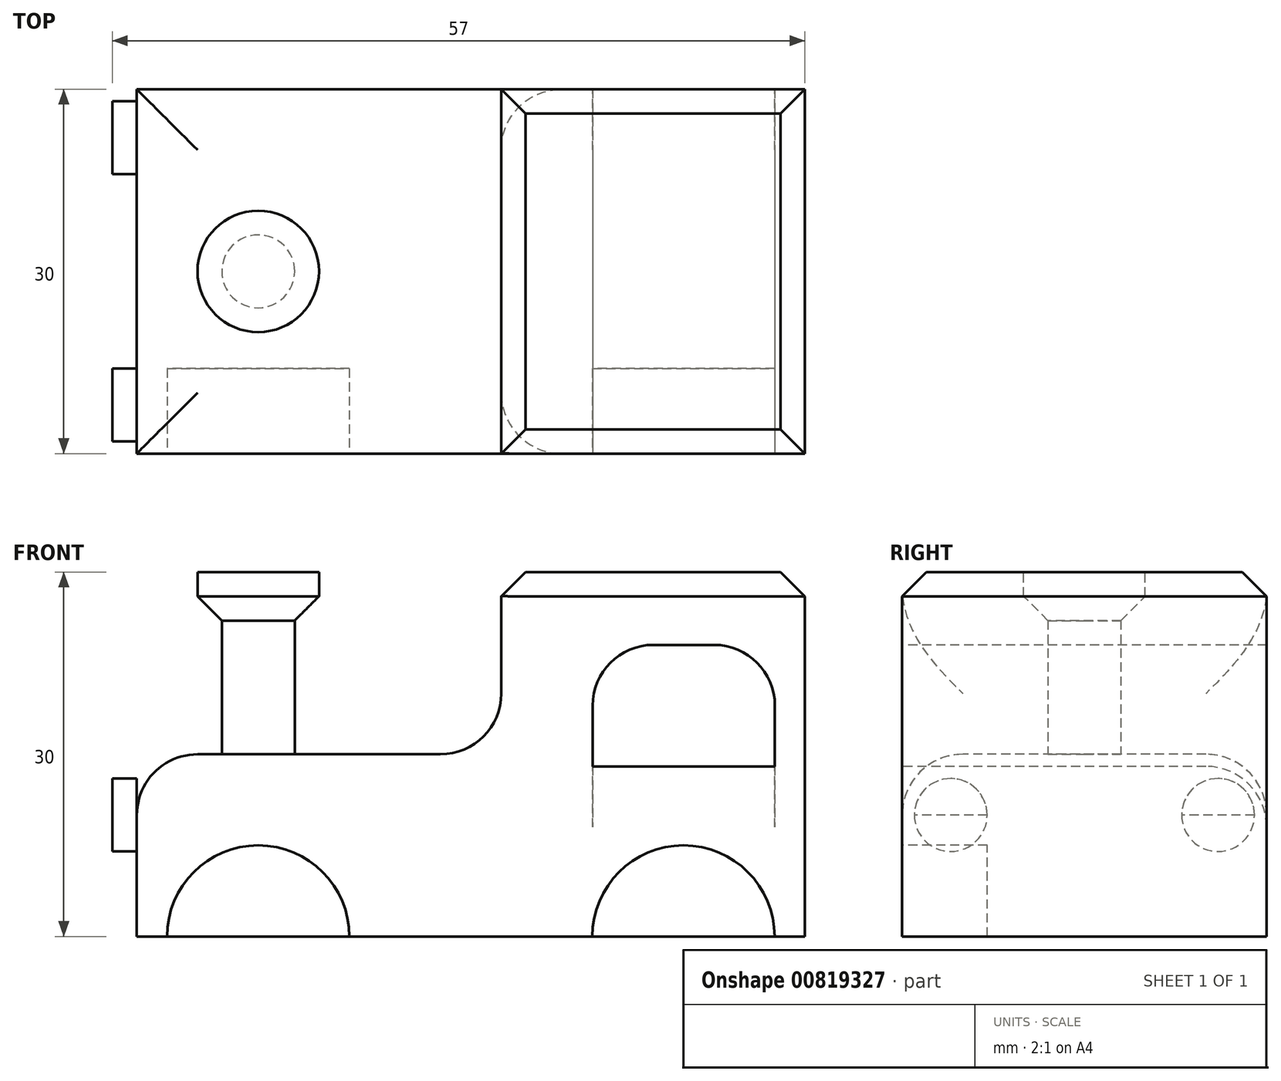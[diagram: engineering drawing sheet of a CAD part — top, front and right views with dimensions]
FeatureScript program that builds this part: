
annotation { "Feature Type Name" : "Feature", "Feature Type Description" : "" }
export const myFeature = defineFeature(function(context is Context, id is Id, definition is map)
    precondition{}
    {
        {
            var Q0;
            Q0=qCreatedBy(makeId("Top.planeOp"),FACE);
            var sketch = newSketch(context, id + "F0", { "sketchPlane" : qUnion([Q0])});
            skLineSegment(sketch, "E0.bottom", {"start": v(-27.5, 15) * mm, "end": v(27.5, 15) * mm});
            skLineSegment(sketch, "E0.top", {"start": v(-27.5, -15) * mm, "end": v(27.5, -15) * mm});
            skLineSegment(sketch, "E0.left", {"start": v(-27.5, 15) * mm, "end": v(-27.5, -15) * mm});
            skLineSegment(sketch, "E0.right", {"start": v(27.5, 15) * mm, "end": v(27.5, -15) * mm});
            skPoint(sketch, "E0.middle", {"position": v(0, 0) * mm});
            skSolve(sketch);
        }
        {
            var Q0;
            Q0 = qSketchRegion(id + "F0", true);
            extrude(context, id + "F1", {"entities" : qUnion([Q0]), "depth" : 30 * mm, "offsetDistance" : 25 * mm});
        }
        {
            var Q0;
            Q0=makeQuery(id+"F1.opExtrude","SWEPT_FACE",FACE,{"disambiguationData":[OSD([sQuery(id+"F0.wireOp",EDGE,"E0.top")])]});
            var sketch = newSketch(context, id + "F2", { "sketchPlane" : qUnion([Q0])});
            skLineSegment(sketch, "E1", {"start": v(-27.5, 15) * mm, "end": v(-27.5, 0) * mm});
            skLineSegment(sketch, "E2", {"start": v(-27.5, 0) * mm, "end": v(27.5, 0) * mm});
            skLineSegment(sketch, "E3", {"start": v(27.5, 0) * mm, "end": v(27.5, 30) * mm});
            skLineSegment(sketch, "E4", {"start": v(27.5, 30) * mm, "end": v(2.5, 30) * mm});
            skLineSegment(sketch, "E5", {"start": v(2.5, 30) * mm, "end": v(2.5, 15) * mm});
            skLineSegment(sketch, "E6", {"start": v(2.5, 15) * mm, "end": v(-27.5, 15) * mm});
            skSolve(sketch);
        }
        {
            var Q0;
            {var subQ0=sQuery(id+"F2.wireOp",EDGE,"E5");Q0=makeQuery(id+"F2.imprint","IMPRINT",FACE,{"disambiguationData":[TD([[makeQuery(id+"F2.imprint","IMPRINT",EDGE,{"derivedFrom":subQ0}),-1.0]])]});}
            extrude(context, id + "F3", {"entities" : qUnion([Q0]), "operationType" : NewBodyOperationType.REMOVE, "endBound" : BoundingType.THROUGH_ALL, "oppositeDirection" : true, "depth" : 25 * mm, "offsetDistance" : 25 * mm});
        }
        {
            var Q0;
            Q0=makeQuery(id+"F1.opExtrude","SWEPT_FACE",FACE,{"disambiguationData":[OSD([sQuery(id+"F0.wireOp",EDGE,"E0.top")])]});
            var sketch = newSketch(context, id + "F4", { "sketchPlane" : qUnion([Q0])});
            skCircle(sketch, "E7", {"center": v(-17.5, 0) * mm, "radius": 7.5 * mm});
            skCircle(sketch, "E8.1.0.0", {"center": v(17.5, 0) * mm, "radius": 7.5 * mm});
            skLineSegment(sketch, "E8.direction1", {"start": v(-17.5, 0) * mm, "end": v(17.5, 0) * mm, "construction": true});
            skSolve(sketch);
        }
        {
            var Q0;
            {var subQ0=sQuery(id+"F4.wireOp",EDGE,"E7");var subQ1=makeQuery(id+"F1.opExtrude","CAP_EDGE",EDGE,{"disambiguationData":[OSD([sQuery(id+"F0.wireOp",EDGE,"E0.top")])],"isStart":true});var subQ2=makeQuery(id+"F4.imprint","INTERSECT",VERTEX,{"disambiguationData":[OD(0.0)],"derivedFrom":[subQ1,subQ0]});Q0=makeQuery(id+"F4.imprint","IMPRINT",FACE,{"disambiguationData":[TD([[makeQuery(id+"F4.imprint","IMPRINT",EDGE,{"disambiguationData":[TD([[subQ2,1.0]])],"derivedFrom":subQ0}),1.0]])]});}
            var Q1;
            {var subQ0=sQuery(id+"F4.wireOp",EDGE,"E8.1.0.0");var subQ1=makeQuery(id+"F1.opExtrude","CAP_EDGE",EDGE,{"disambiguationData":[OSD([sQuery(id+"F0.wireOp",EDGE,"E0.top")])],"isStart":true});var subQ2=makeQuery(id+"F4.imprint","INTERSECT",VERTEX,{"disambiguationData":[OD(0.0)],"derivedFrom":[subQ1,subQ0]});Q1=makeQuery(id+"F4.imprint","IMPRINT",FACE,{"disambiguationData":[TD([[makeQuery(id+"F4.imprint","IMPRINT",EDGE,{"disambiguationData":[TD([[subQ2,-1.0]])],"derivedFrom":subQ0}),1.0]])]});}
            extrude(context, id + "F5", {"entities" : qUnion([Q0, Q1]), "operationType" : NewBodyOperationType.REMOVE, "oppositeDirection" : true, "depth" : 7 * mm, "offsetDistance" : 25 * mm});
        }
        {
            var Q0;
            Q0=makeQuery(id+"F3.boolean.opBoolean","COPY",FACE,{"derivedFrom":makeQuery(id+"F3.opExtrude","SWEPT_FACE",FACE,{"disambiguationData":[OSD([sQuery(id+"F2.wireOp",EDGE,"E6")])]})});
            fillet(context, id + "F6", {"entities" : qUnion([Q0]), "radius" : 5 * mm, "tangentPropagation" : true, "allowEdgeOverflow" : false});
        }
        {
            var Q0;
            Q0=makeQuery(id+"F1.opExtrude","CAP_FACE",FACE,{"disambiguationData":[OSD([sQuery(id+"F0.wireOp",EDGE,"E0.bottom"),sQuery(id+"F0.wireOp",EDGE,"E0.top"),sQuery(id+"F0.wireOp",EDGE,"E0.left"),sQuery(id+"F0.wireOp",EDGE,"E0.right")])],"isStart":false});
            chamfer(context, id + "F7", {"entities" : qUnion([Q0]), "width" : 2 * mm, "tangentPropagation" : true});
        }
        {
            var Q0;
            Q0=makeQuery(id+"F1.opExtrude","SWEPT_FACE",FACE,{"disambiguationData":[OSD([sQuery(id+"F0.wireOp",EDGE,"E0.top")])]});
            var sketch = newSketch(context, id + "F8", { "sketchPlane" : qUnion([Q0])});
            skPoint(sketch, "E9.cornerSnap0", {"position": v(7.5, 24) * mm});
            skLineSegment(sketch, "E10.bottom", {"start": v(15.02, 24) * mm, "end": v(20.02, 24) * mm});
            skLineSegment(sketch, "E10.top", {"start": v(10.02, 14) * mm, "end": v(25.02, 14) * mm});
            skLineSegment(sketch, "E10.left", {"start": v(10.02, 19) * mm, "end": v(10.02, 14) * mm});
            skLineSegment(sketch, "E10.right", {"start": v(25.02, 19) * mm, "end": v(25.02, 14) * mm});
            skPoint(sketch, "E11.visualSharp", {"position": v(10.02, 24) * mm});
            skArc(sketch, "E11.filletArc", {"start": v(15.02, 24) * mm, "mid": v(11.49, 22.54) * mm, "end": v(10.02, 19) * mm});
            skPoint(sketch, "E12.visualSharp", {"position": v(25.02, 24) * mm});
            skArc(sketch, "E12.filletArc", {"start": v(25.02, 19) * mm, "mid": v(23.56, 22.54) * mm, "end": v(20.02, 24) * mm});
            skSolve(sketch);
        }
        {
            var Q0;
            Q0=makeQuery(id+"F8.imprint","IMPRINT",FACE,{"disambiguationData":[TD([[makeQuery(id+"F8.imprint","IMPRINT",EDGE,{"derivedFrom":sQuery(id+"F8.wireOp",EDGE,"E10.bottom")}),-1.0]])]});
            extrude(context, id + "F9", {"entities" : qUnion([Q0]), "operationType" : NewBodyOperationType.REMOVE, "endBound" : BoundingType.THROUGH_ALL, "oppositeDirection" : true, "depth" : 25 * mm, "offsetDistance" : 25 * mm});
        }
        {
            var Q0;
            Q0=makeQuery(id+"F9.boolean.opBoolean","COPY",EDGE,{"derivedFrom":makeQuery(id+"F9.opExtrude","CAP_EDGE",EDGE,{"disambiguationData":[OSD([sQuery(id+"F8.wireOp",EDGE,"E10.top")])],"isStart":true})});
            var Q1;
            Q1=makeQuery(id+"F9.boolean.opBoolean","INTERSECT",EDGE,{"derivedFrom":[makeQuery(id+"F1.opExtrude","SWEPT_FACE",FACE,{"disambiguationData":[OSD([sQuery(id+"F0.wireOp",EDGE,"E0.bottom")])]}),makeQuery(id+"F9.opExtrude","SWEPT_FACE",FACE,{"disambiguationData":[OSD([sQuery(id+"F8.wireOp",EDGE,"E10.top")])]})]});
            fillet(context, id + "F10", {"entities" : qUnion([Q0, Q1]), "radius" : 5 * mm, "tangentPropagation" : true, "allowEdgeOverflow" : false});
        }
        {
            var Q0;
            Q0=makeQuery(id+"F1.opExtrude","SWEPT_FACE",FACE,{"disambiguationData":[OSD([sQuery(id+"F0.wireOp",EDGE,"E0.left")])]});
            var sketch = newSketch(context, id + "F11", { "sketchPlane" : qUnion([Q0])});
            skCircle(sketch, "E13", {"center": v(-11, 10) * mm, "radius": 3 * mm});
            skCircle(sketch, "E14", {"center": v(11, 10) * mm, "radius": 3 * mm});
            skSolve(sketch);
        }
        {
            var Q0;
            {var subQ0=sQuery(id+"F11.wireOp",EDGE,"E13");var subQ1=sQuery(id+"F0.wireOp",EDGE,"E0.left");var subQ2=makeQuery(id+"F6.opFillet","BLEND_EDGE",EDGE,{"blendedFrom":[makeQuery(id+"F3.boolean.opBoolean","COPY",EDGE,{"derivedFrom":makeQuery(id+"F3.opExtrude","SWEPT_EDGE",EDGE,{"disambiguationData":[OSD([sQuery(id+"F0.wireOp",EDGE,"E0.top"),subQ1,sQuery(id+"F2.wireOp",EDGE,"E1"),sQuery(id+"F2.wireOp",EDGE,"E6")])]})}),makeQuery(id+"F1.opExtrude","SWEPT_FACE",FACE,{"disambiguationData":[OSD([subQ1])]})],"blendedInto":[makeQuery(id+"F1.opExtrude","SWEPT_FACE",FACE,{"disambiguationData":[OSD([subQ1])]})]});var subQ3=makeQuery(id+"F11.imprint","INTERSECT",VERTEX,{"disambiguationData":[OD(0.0)],"derivedFrom":[subQ2,subQ0]});Q0=makeQuery(id+"F11.imprint","IMPRINT",FACE,{"disambiguationData":[TD([[makeQuery(id+"F11.imprint","IMPRINT",EDGE,{"disambiguationData":[TD([[subQ3,-1.0]])],"derivedFrom":subQ0}),1.0]])]});}
            var Q1;
            {var subQ0=sQuery(id+"F11.wireOp",EDGE,"E13");var subQ1=sQuery(id+"F0.wireOp",EDGE,"E0.left");var subQ2=makeQuery(id+"F6.opFillet","BLEND_EDGE",EDGE,{"blendedFrom":[makeQuery(id+"F3.boolean.opBoolean","COPY",EDGE,{"derivedFrom":makeQuery(id+"F3.opExtrude","SWEPT_EDGE",EDGE,{"disambiguationData":[OSD([sQuery(id+"F0.wireOp",EDGE,"E0.top"),subQ1,sQuery(id+"F2.wireOp",EDGE,"E1"),sQuery(id+"F2.wireOp",EDGE,"E6")])]})}),makeQuery(id+"F1.opExtrude","SWEPT_FACE",FACE,{"disambiguationData":[OSD([subQ1])]})],"blendedInto":[makeQuery(id+"F1.opExtrude","SWEPT_FACE",FACE,{"disambiguationData":[OSD([subQ1])]})]});var subQ3=makeQuery(id+"F11.imprint","INTERSECT",VERTEX,{"disambiguationData":[OD(0.0)],"derivedFrom":[subQ2,subQ0]});Q1=makeQuery(id+"F11.imprint","IMPRINT",FACE,{"disambiguationData":[TD([[makeQuery(id+"F11.imprint","IMPRINT",EDGE,{"disambiguationData":[TD([[subQ3,1.0]])],"derivedFrom":subQ0}),1.0]])]});}
            var Q2;
            {var subQ0=sQuery(id+"F11.wireOp",EDGE,"E14");var subQ1=sQuery(id+"F0.wireOp",EDGE,"E0.left");var subQ2=makeQuery(id+"F6.opFillet","BLEND_EDGE",EDGE,{"blendedFrom":[makeQuery(id+"F3.boolean.opBoolean","COPY",EDGE,{"derivedFrom":makeQuery(id+"F3.opExtrude","SWEPT_EDGE",EDGE,{"disambiguationData":[OSD([sQuery(id+"F0.wireOp",EDGE,"E0.top"),subQ1,sQuery(id+"F2.wireOp",EDGE,"E1"),sQuery(id+"F2.wireOp",EDGE,"E6")])]})}),makeQuery(id+"F1.opExtrude","SWEPT_FACE",FACE,{"disambiguationData":[OSD([subQ1])]})],"blendedInto":[makeQuery(id+"F1.opExtrude","SWEPT_FACE",FACE,{"disambiguationData":[OSD([subQ1])]})]});var subQ3=makeQuery(id+"F11.imprint","INTERSECT",VERTEX,{"disambiguationData":[OD(0.0)],"derivedFrom":[subQ2,subQ0]});Q2=makeQuery(id+"F11.imprint","IMPRINT",FACE,{"disambiguationData":[TD([[makeQuery(id+"F11.imprint","IMPRINT",EDGE,{"disambiguationData":[TD([[subQ3,1.0]])],"derivedFrom":subQ0}),1.0]])]});}
            var Q3;
            {var subQ0=sQuery(id+"F11.wireOp",EDGE,"E14");var subQ1=sQuery(id+"F0.wireOp",EDGE,"E0.left");var subQ2=makeQuery(id+"F6.opFillet","BLEND_EDGE",EDGE,{"blendedFrom":[makeQuery(id+"F3.boolean.opBoolean","COPY",EDGE,{"derivedFrom":makeQuery(id+"F3.opExtrude","SWEPT_EDGE",EDGE,{"disambiguationData":[OSD([sQuery(id+"F0.wireOp",EDGE,"E0.top"),subQ1,sQuery(id+"F2.wireOp",EDGE,"E1"),sQuery(id+"F2.wireOp",EDGE,"E6")])]})}),makeQuery(id+"F1.opExtrude","SWEPT_FACE",FACE,{"disambiguationData":[OSD([subQ1])]})],"blendedInto":[makeQuery(id+"F1.opExtrude","SWEPT_FACE",FACE,{"disambiguationData":[OSD([subQ1])]})]});var subQ3=makeQuery(id+"F11.imprint","INTERSECT",VERTEX,{"disambiguationData":[OD(0.0)],"derivedFrom":[subQ2,subQ0]});Q3=makeQuery(id+"F11.imprint","IMPRINT",FACE,{"disambiguationData":[TD([[makeQuery(id+"F11.imprint","IMPRINT",EDGE,{"disambiguationData":[TD([[subQ3,-1.0]])],"derivedFrom":subQ0}),1.0]])]});}
            var Q4;
            Q4=sQuery(id+"F11.wireOp",EDGE,"E13");
            var Q5;
            Q5=sQuery(id+"F11.wireOp",EDGE,"E14");
            extrude(context, id + "F12", {"entities" : qUnion([Q0, Q1, Q2, Q3]), "operationType" : NewBodyOperationType.ADD, "surfaceEntities" : qUnion([Q4, Q5]), "depth" : 2 * mm, "offsetDistance" : 25 * mm});
        }
        {
            var Q0;
            Q0=makeQuery(id+"F3.boolean.opBoolean","COPY",FACE,{"derivedFrom":makeQuery(id+"F3.opExtrude","SWEPT_FACE",FACE,{"disambiguationData":[OSD([sQuery(id+"F2.wireOp",EDGE,"E6")])]})});
            var sketch = newSketch(context, id + "F13", { "sketchPlane" : qUnion([Q0])});
            skCircle(sketch, "E15", {"center": v(-17.5, 0) * mm, "radius": 3 * mm});
            skSolve(sketch);
        }
        {
            var Q0;
            Q0=makeQuery(id+"F13.imprint","IMPRINT",FACE,{"disambiguationData":[TD([[makeQuery(id+"F13.imprint","IMPRINT",EDGE,{"derivedFrom":sQuery(id+"F13.wireOp",EDGE,"E15")}),1.0]])]});
            var Q1;
            Q1=sQuery(id+"F13.wireOp",EDGE,"E15");
            extrude(context, id + "F14", {"entities" : qUnion([Q0]), "operationType" : NewBodyOperationType.ADD, "surfaceEntities" : qUnion([Q1]), "depth" : 15 * mm, "offsetDistance" : 25 * mm});
        }
        {
            var Q0;
            Q0=makeQuery(id+"F14.opExtrude","CAP_FACE",FACE,{"disambiguationData":[OSD([sQuery(id+"F13.wireOp",EDGE,"E15")])],"isStart":false});
            var sketch = newSketch(context, id + "F15", { "sketchPlane" : qUnion([Q0])});
            skCircle(sketch, "E16", {"center": v(-17.5, 0) * mm, "radius": 5 * mm});
            skSolve(sketch);
        }
        {
            var Q0;
            Q0=makeQuery(id+"F15.imprint","IMPRINT",FACE,{"disambiguationData":[TD([[makeQuery(id+"F15.imprint","IMPRINT",EDGE,{"derivedFrom":sQuery(id+"F15.wireOp",EDGE,"E16")}),1.0]])]});
            extrude(context, id + "F16", {"entities" : qUnion([Q0]), "operationType" : NewBodyOperationType.ADD, "oppositeDirection" : true, "depth" : 4 * mm, "offsetDistance" : 25 * mm});
        }
        {
            var Q0;
            Q0=makeQuery(id+"F16.opExtrude","CAP_EDGE",EDGE,{"disambiguationData":[OSD([sQuery(id+"F15.wireOp",EDGE,"E16")])],"isStart":false});
            chamfer(context, id + "F17", {"entities" : qUnion([Q0]), "width" : 2 * mm, "tangentPropagation" : true});
        }
    });
